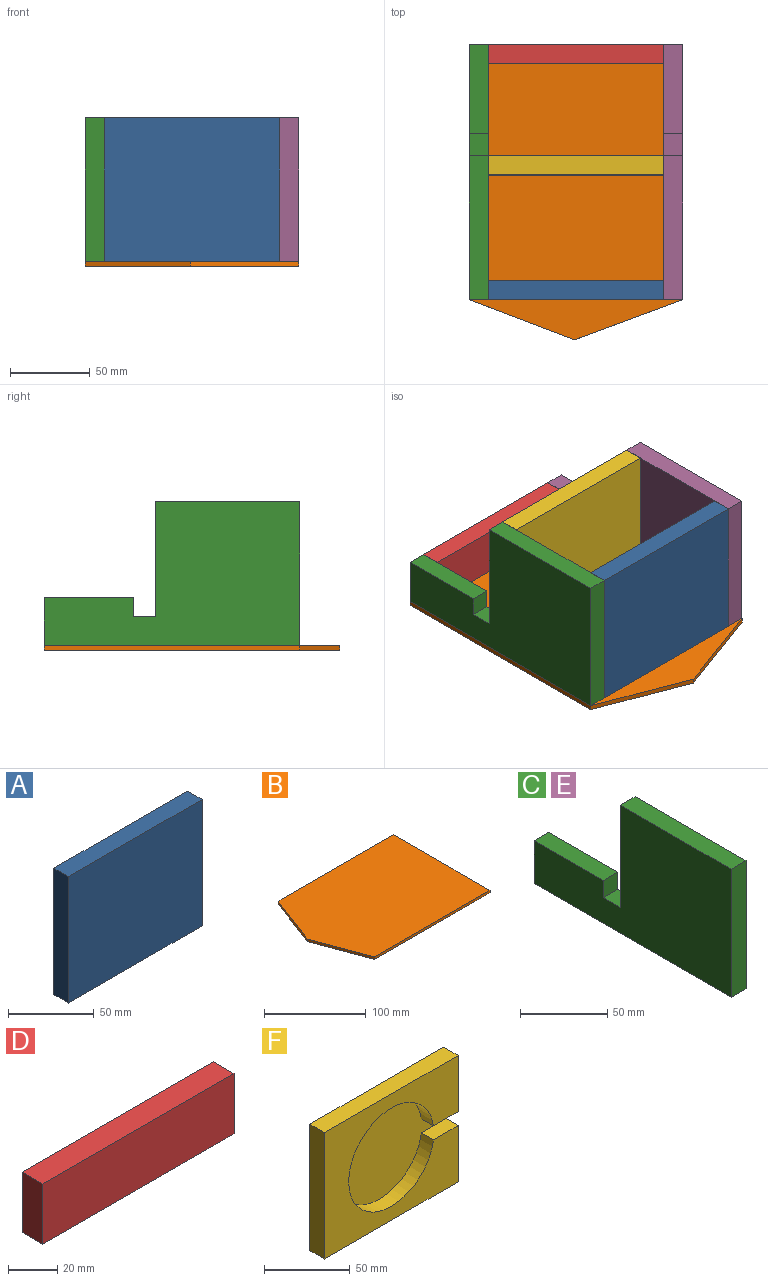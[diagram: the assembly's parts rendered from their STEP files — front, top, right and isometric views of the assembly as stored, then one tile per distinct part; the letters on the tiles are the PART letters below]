
ASSEMBLY  parts=6 mates=5
PART A: 6 faces, bbox 110x12x90 mm
  f0: plane 110x12mm, normal (0,0,1), area 1320mm2, adj f1,f3,f4,f5
  f1: plane 90x12mm, normal (-1,0,0), area 1080mm2, adj f0,f2,f4,f5
  f2: plane 110x12mm, normal (0,0,-1), area 1320mm2, adj f1,f3,f4,f5
  f3: plane 90x12mm, normal (1,0,0), area 1080mm2, adj f0,f2,f4,f5
  f4: plane 110x90mm, normal (0,-1,0), area 9900mm2, adj f0,f1,f2,f3
  f5: plane 110x90mm, normal (0,1,0), area 9900mm2, adj f0,f1,f2,f3
PART B: 7 faces, bbox 185.1x134x3 mm
  f0: plane 134x3mm, normal (1,0,0), area 402mm2, adj f1,f4,f5,f6
  f1: plane 160x3mm, normal (0,1,0), area 480mm2, adj f0,f2,f5,f6
  f2: plane 66x25.12mm, normal (-0.93,0.36,0), area 211.9mm2, adj f1,f3,f5,f6
  f3: plane 68x25.12mm, normal (-0.94,-0.35,0), area 217.5mm2, adj f2,f4,f5,f6
  f4: plane 160x3mm, normal (0,-1,0), area 480mm2, adj f0,f3,f5,f6
  f5: plane 185.12x134mm, normal (0,0,1), area 23122.9mm2, adj f0,f1,f2,f3,f4
  f6: plane 185.12x134mm, normal (0,0,-1), area 23122.9mm2, adj f0,f1,f2,f3,f4
PART C: 10 faces, bbox 12x160x90 mm
  f0: plane 90x12mm, normal (0,0,1), area 1080mm2, adj f1,f7,f8,f9
  f1: plane 90x12mm, normal (0,-1,0), area 1080mm2, adj f0,f2,f8,f9
  f2: plane 160x12mm, normal (0,0,-1), area 1920mm2, adj f1,f3,f8,f9
  f3: plane 30x12mm, normal (0,1,0), area 360mm2, adj f2,f4,f8,f9
  f4: plane 56x12mm, normal (0,0,1), area 672mm2, adj f3,f5,f8,f9
  f5: plane 12x12mm, normal (0,-1,0), area 144mm2, adj f4,f6,f8,f9
  f6: plane 14x12mm, normal (0,0,1), area 168mm2, adj f5,f7,f8,f9
  f7: plane 72x12mm, normal (0,1,0), area 864mm2, adj f0,f6,f8,f9
  f8: plane 160x90mm, normal (1,0,0), area 10032mm2, adj f0,f1,f2,f3,f4,f5,f6,f7
  f9: plane 160x90mm, normal (-1,0,0), area 10032mm2, adj f0,f1,f2,f3,f4,f5,f6,f7
PART D: 6 faces, bbox 110x12x30 mm
  f0: plane 110x12mm, normal (0,0,1), area 1320mm2, adj f1,f3,f4,f5
  f1: plane 30x12mm, normal (-1,0,0), area 360mm2, adj f0,f2,f4,f5
  f2: plane 110x12mm, normal (0,0,-1), area 1320mm2, adj f1,f3,f4,f5
  f3: plane 30x12mm, normal (1,0,0), area 360mm2, adj f0,f2,f4,f5
  f4: plane 110x30mm, normal (0,-1,0), area 3300mm2, adj f0,f1,f2,f3
  f5: plane 110x30mm, normal (0,1,0), area 3300mm2, adj f0,f1,f2,f3
PART E: same geometry as C
PART F: 10 faces, bbox 110x12x90 mm
  f0: plane 90x12mm, normal (1,0,0), area 980.2mm2, adj f1,f2,f4,f5,f6,f8,f9
  f1: plane 110x90mm, normal (0,-1,0), area 5850.8mm2, adj f0,f2,f3,f4,f6,f7,f8
  f2: plane 110x12mm, normal (0,0,1), area 1320mm2, adj f0,f1,f3,f5
  f3: plane 90x12mm, normal (-1,0,0), area 1080mm2, adj f1,f2,f4,f5
  f4: plane 110x12mm, normal (0,0,-1), area 1320mm2, adj f0,f1,f3,f5
  f5: plane 110x90mm, normal (0,1,0), area 9900mm2, adj f0,f2,f3,f4
  f6: plane 20.36x10mm, normal (0,0,-1), area 203.6mm2, adj f0,f1,f7,f9
  f7: cylinder r=35mm len=70mm, axis (0,-1,0), area 2099mm2, adj f1,f6,f8,f9
  f8: plane 20.36x10mm, normal (0,0,1), area 203.6mm2, adj f0,f1,f7,f9
  f9: plane 90x70mm, normal (0,-1,0), area 4049.2mm2, adj f0,f6,f7,f8
PLACE A t=(31,-111.92,8.16)mm
PLACE B rot(axis=(0,0,1),90deg) t=(-6.32,-55.2,-20.94)mm
PLACE C rot(axis=(0,1,0),0deg) t=(-56.11,-52.96,21.62)mm
PLACE D t=(31,36.08,8.16)mm
PLACE E t=(65.89,-52.96,21.62)mm
PLACE F rot(axis=(0,0,1),180deg) t=(-9.22,-45.92,8.16)mm
MATE fastened C.f8 <-> F.f0  axis (1,0,0) through (-44.11,-33.92,72.06)mm
MATE fastened A.f3 <-> E.f9  axis (1,0,0) through (65.89,-123.92,27.06)mm
MATE fastened C.f2 <-> B.f5  axis (0,0,-1) through (-56.11,36.08,-17.94)mm
MATE fastened C.f8 <-> D.f1  axis (1,0,0) through (-44.11,36.08,-2.94)mm
MATE fastened C.f8 <-> A.f1  axis (1,0,0) through (-44.11,-123.92,27.06)mm
